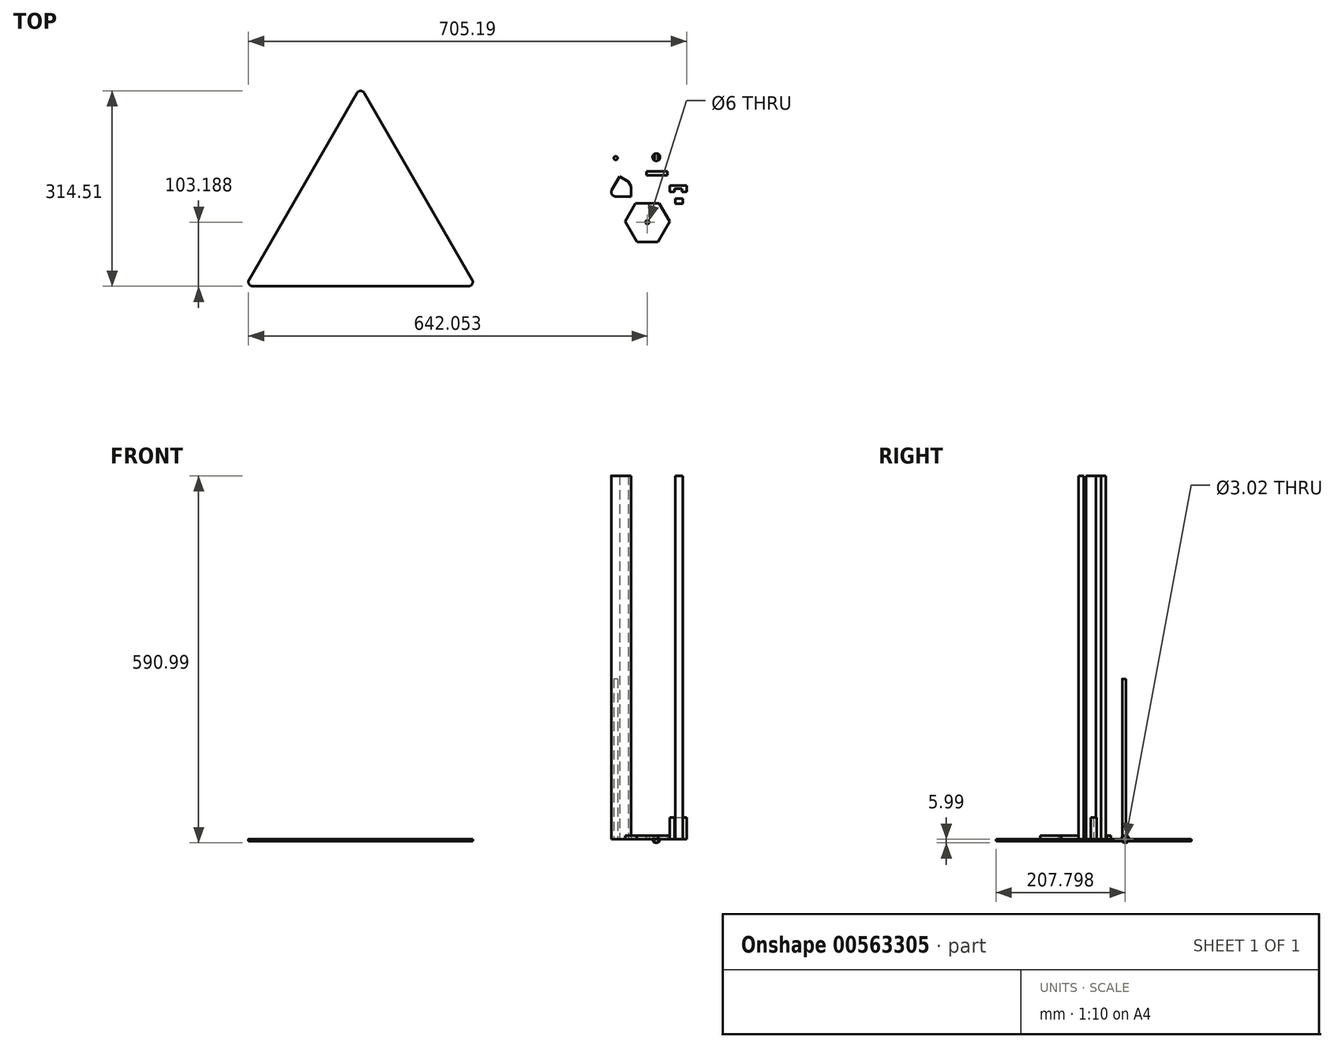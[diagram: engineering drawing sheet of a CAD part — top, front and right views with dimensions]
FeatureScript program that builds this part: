
annotation { "Feature Type Name" : "Feature", "Feature Type Description" : "" }
export const myFeature = defineFeature(function(context is Context, id is Id, definition is map)
    precondition{}
    {
        {
            var Q0;
            Q0=qCreatedBy(makeId("Top.planeOp"),FACE);
            var sketch = newSketch(context, id + "F0", { "sketchPlane" : qUnion([Q0])});
            skLineSegment(sketch, "E0", {"start": v(-31.56, -27.8) * mm, "end": v(-6.56, -27.8) * mm});
            skLineSegment(sketch, "E1", {"start": v(-37.63, -17.3) * mm, "end": v(-25.13, 4.35) * mm});
            skPoint(sketch, "E2.visualSharp", {"position": v(-43.69, -27.8) * mm});
            skArc(sketch, "E2.filletArc", {"start": v(-37.63, -17.3) * mm, "mid": v(-37.63, -24.3) * mm, "end": v(-31.56, -27.8) * mm});
            skLineSegment(sketch, "E3", {"start": v(-6.56, -27.8) * mm, "end": v(-6.56, -11.8) * mm});
            skLineSegment(sketch, "E4", {"start": v(-25.13, 4.35) * mm, "end": v(-11.27, -3.65) * mm});
            skLineSegment(sketch, "E5", {"start": v(-11.27, -3.65) * mm, "end": v(-6.56, -11.8) * mm});
            skSolve(sketch);
        }
        {
            var Q0;
            Q0=makeQuery(id+"F0.imprint","IMPRINT",FACE,{"disambiguationData":[TD([[makeQuery(id+"F0.imprint","IMPRINT",EDGE,{"derivedFrom":sQuery(id+"F0.wireOp",EDGE,"E0")}),1.0]])]});
            extrude(context, id + "F1", {"entities" : qUnion([Q0]), "depth" : 585 * mm, "offsetDistance" : 25 * mm});
        }
        {
            var Q0;
            Q0=qCreatedBy(makeId("Top.planeOp"),FACE);
            var sketch = newSketch(context, id + "F2", { "sketchPlane" : qUnion([Q0])});
            skLineSegment(sketch, "E6.bottom", {"start": v(64.17, -31.27) * mm, "end": v(76.17, -31.27) * mm});
            skLineSegment(sketch, "E6.top", {"start": v(64.17, -39.27) * mm, "end": v(76.17, -39.27) * mm});
            skLineSegment(sketch, "E6.left", {"start": v(64.17, -31.27) * mm, "end": v(64.17, -39.27) * mm});
            skLineSegment(sketch, "E6.right", {"start": v(76.17, -31.27) * mm, "end": v(76.17, -39.27) * mm});
            skSolve(sketch);
        }
        {
            var Q0;
            Q0 = qSketchRegion(id + "F2", true);
            extrude(context, id + "F3", {"entities" : qUnion([Q0]), "depth" : 585 * mm, "offsetDistance" : 25 * mm});
        }
        {
            var Q0;
            Q0=qCreatedBy(makeId("Top.planeOp"),FACE);
            var sketch = newSketch(context, id + "F4", { "sketchPlane" : qUnion([Q0])});
            skLineSegment(sketch, "E7.bottom", {"start": v(55.7, -10.12) * mm, "end": v(82.7, -10.12) * mm});
            skLineSegment(sketch, "E7.left", {"start": v(55.7, -10.12) * mm, "end": v(55.7, -20.12) * mm});
            skLineSegment(sketch, "E7.right", {"start": v(82.7, -10.12) * mm, "end": v(82.7, -20.12) * mm});
            skLineSegment(sketch, "E8", {"start": v(63.2, -20.12) * mm, "end": v(63.2, -15.12) * mm});
            skLineSegment(sketch, "E9", {"start": v(75.2, -15.12) * mm, "end": v(75.2, -20.12) * mm});
            skLineSegment(sketch, "E10", {"start": v(63.2, -15.12) * mm, "end": v(75.2, -15.12) * mm});
            skLineSegment(sketch, "E11", {"start": v(55.7, -20.12) * mm, "end": v(63.2, -20.12) * mm});
            skLineSegment(sketch, "E12", {"start": v(75.2, -20.12) * mm, "end": v(82.7, -20.12) * mm});
            skSolve(sketch);
        }
        {
            var Q0;
            Q0=makeQuery(id+"F4.imprint","IMPRINT",FACE,{"disambiguationData":[TD([[makeQuery(id+"F4.imprint","IMPRINT",EDGE,{"derivedFrom":sQuery(id+"F4.wireOp",EDGE,"E7.bottom")}),-1.0]])]});
            extrude(context, id + "F5", {"entities" : qUnion([Q0]), "depth" : 34.7 * mm, "offsetDistance" : 25 * mm});
        }
        {
            var Q0;
            Q0=qCreatedBy(makeId("Top.planeOp"),FACE);
            var sketch = newSketch(context, id + "F6", { "sketchPlane" : qUnion([Q0])});
            skCircle(sketch, "E13", {"center": v(33.81, 35.39) * mm, "radius": 6 * mm});
            skLineSegment(sketch, "E14.bottom", {"start": v(36.81, 24.39) * mm, "end": v(30.81, 24.39) * mm});
            skLineSegment(sketch, "E14.top", {"start": v(36.81, 46.39) * mm, "end": v(30.81, 46.39) * mm});
            skLineSegment(sketch, "E14.left", {"start": v(36.81, 24.39) * mm, "end": v(36.81, 46.39) * mm});
            skLineSegment(sketch, "E14.right", {"start": v(30.81, 24.39) * mm, "end": v(30.81, 46.39) * mm});
            skLineSegment(sketch, "E15.bottom", {"start": v(36.81, 36.89) * mm, "end": v(30.81, 36.89) * mm});
            skLineSegment(sketch, "E15.top", {"start": v(36.81, 33.89) * mm, "end": v(30.81, 33.89) * mm});
            skLineSegment(sketch, "E15.left", {"start": v(36.81, 36.89) * mm, "end": v(36.81, 33.89) * mm});
            skLineSegment(sketch, "E15.right", {"start": v(30.81, 36.89) * mm, "end": v(30.81, 33.89) * mm});
            skLineSegment(sketch, "E16", {"start": v(27.81, 35.38) * mm, "end": v(42.26, 35.38) * mm, "construction": true});
            skSolve(sketch);
        }
        {
            var Q0;
            {var subQ5=sQuery(id+"F6.wireOp",EDGE,"E15.bottom");Q0=makeQuery(id+"F6.imprint","IMPRINT",FACE,{"disambiguationData":[TD([[makeQuery(id+"F6.imprint","IMPRINT",EDGE,{"derivedFrom":subQ5}),-1.0]])]});}
            var Q1;
            Q1=sQuery(id+"F6.wireOp",EDGE,"E16");
            revolve(context, id + "F7", {"entities" : qUnion([Q0]), "axis" : qUnion([Q1]), "revolveType" : RevolveType.FULL});
        }
        {
            var Q0;
            Q0=qCreatedBy(makeId("Top.planeOp"),FACE);
            var sketch = newSketch(context, id + "F8", { "sketchPlane" : qUnion([Q0])});
            skCircle(sketch, "E17", {"center": v(-31.41, 33.89) * mm, "radius": 3 * mm});
            skSolve(sketch);
        }
        {
            var Q0;
            Q0=makeQuery(id+"F8.imprint","IMPRINT",FACE,{"disambiguationData":[TD([[makeQuery(id+"F8.imprint","IMPRINT",EDGE,{"derivedFrom":sQuery(id+"F8.wireOp",EDGE,"E17")}),1.0]])]});
            extrude(context, id + "F9", {"entities" : qUnion([Q0]), "depth" : 258 * mm, "offsetDistance" : 25 * mm});
        }
        {
            var Q0;
            Q0=qCreatedBy(makeId("Top.planeOp"),FACE);
            var sketch = newSketch(context, id + "F10", { "sketchPlane" : qUnion([Q0])});
            skLineSegment(sketch, "E18.bottom", {"start": v(51.8, 6.41) * mm, "end": v(17.8, 6.41) * mm});
            skLineSegment(sketch, "E18.top", {"start": v(51.8, 12.41) * mm, "end": v(17.8, 12.41) * mm});
            skLineSegment(sketch, "E18.left", {"start": v(51.8, 6.41) * mm, "end": v(51.8, 12.41) * mm});
            skLineSegment(sketch, "E18.right", {"start": v(17.8, 6.41) * mm, "end": v(17.8, 12.41) * mm});
            skPoint(sketch, "E18.middle", {"position": v(34.8, 9.41) * mm});
            skSolve(sketch);
        }
        {
            var Q0;
            Q0=makeQuery(id+"F10.imprint","IMPRINT",FACE,{"disambiguationData":[TD([[makeQuery(id+"F10.imprint","IMPRINT",EDGE,{"derivedFrom":sQuery(id+"F10.wireOp",EDGE,"E18.bottom")}),-1.0]])]});
            extrude(context, id + "F11", {"entities" : qUnion([Q0]), "depth" : 6 * mm, "offsetDistance" : 25 * mm});
        }
        {
            var Q0;
            Q0=qCreatedBy(makeId("Top.planeOp"),FACE);
            var sketch = newSketch(context, id + "F12", { "sketchPlane" : qUnion([Q0])});
            skLineSegment(sketch, "E19", {"start": v(2.57, -100.99) * mm, "end": v(36.57, -100.99) * mm});
            skLineSegment(sketch, "E20", {"start": v(36.57, -100.99) * mm, "end": v(55.57, -68.08) * mm});
            skLineSegment(sketch, "E21", {"start": v(55.57, -68.08) * mm, "end": v(38.57, -38.63) * mm});
            skLineSegment(sketch, "E22", {"start": v(38.57, -38.63) * mm, "end": v(0.57, -38.63) * mm});
            skLineSegment(sketch, "E23", {"start": v(0.57, -38.63) * mm, "end": v(-16.43, -68.08) * mm});
            skLineSegment(sketch, "E24", {"start": v(-16.43, -68.08) * mm, "end": v(2.57, -100.99) * mm});
            skLineSegment(sketch, "E25", {"start": v(19.57, -38.63) * mm, "end": v(19.57, -100.99) * mm, "construction": true});
            skLineSegment(sketch, "E26", {"start": v(-6.93, -84.53) * mm, "end": v(47.07, -53.35) * mm, "construction": true});
            skLineSegment(sketch, "E27", {"start": v(-7.93, -53.35) * mm, "end": v(46.07, -84.53) * mm, "construction": true});
            skPoint(sketch, "E28", {"position": v(19.57, -69.23) * mm});
            skCircle(sketch, "E29", {"center": v(19.57, -69.23) * mm, "radius": 3 * mm});
            skSolve(sketch);
        }
        {
            var Q0;
            Q0 = qSketchRegion(id + "F12", true);
            extrude(context, id + "F13", {"entities" : qUnion([Q0]), "depth" : 6 * mm, "offsetDistance" : 25 * mm});
        }
        {
            var Q0;
            Q0=qCreatedBy(makeId("Top.planeOp"),FACE);
            var sketch = newSketch(context, id + "F14", { "sketchPlane" : qUnion([Q0])});
            skLineSegment(sketch, "E30", {"start": v(-448.04, 138.6) * mm, "end": v(-460.54, 116.94) * mm});
            skLineSegment(sketch, "E31", {"start": v(-435.92, 138.6) * mm, "end": v(-423.42, 116.94) * mm});
            skPoint(sketch, "E32.visualSharp", {"position": v(-441.98, 149.1) * mm});
            skArc(sketch, "E32.filletArc", {"start": v(-435.92, 138.6) * mm, "mid": v(-441.98, 142.1) * mm, "end": v(-448.04, 138.6) * mm});
            skLineSegment(sketch, "E33", {"start": v(-460.54, 116.94) * mm, "end": v(-446.69, 108.94) * mm});
            skLineSegment(sketch, "E34", {"start": v(-423.42, 116.94) * mm, "end": v(-437.28, 108.94) * mm});
            skLineSegment(sketch, "E35", {"start": v(-437.28, 108.94) * mm, "end": v(-446.69, 108.94) * mm});
            skLineSegment(sketch, "E36", {"start": v(-615.48, -172.42) * mm, "end": v(-590.48, -172.42) * mm});
            skLineSegment(sketch, "E37", {"start": v(-621.54, -161.92) * mm, "end": v(-609.04, -140.27) * mm});
            skPoint(sketch, "E38.visualSharp", {"position": v(-627.6, -172.42) * mm});
            skArc(sketch, "E38.filletArc", {"start": v(-621.54, -161.92) * mm, "mid": v(-621.54, -168.92) * mm, "end": v(-615.48, -172.42) * mm});
            skLineSegment(sketch, "E39", {"start": v(-590.48, -172.42) * mm, "end": v(-590.48, -156.42) * mm});
            skLineSegment(sketch, "E40", {"start": v(-609.04, -140.27) * mm, "end": v(-595.19, -148.27) * mm});
            skLineSegment(sketch, "E41", {"start": v(-595.19, -148.27) * mm, "end": v(-590.48, -156.42) * mm});
            skLineSegment(sketch, "E42", {"start": v(-262.42, -161.92) * mm, "end": v(-274.92, -140.27) * mm});
            skLineSegment(sketch, "E43", {"start": v(-268.48, -172.42) * mm, "end": v(-293.48, -172.42) * mm});
            skPoint(sketch, "E44.visualSharp", {"position": v(-256.36, -172.42) * mm});
            skArc(sketch, "E44.filletArc", {"start": v(-268.48, -172.42) * mm, "mid": v(-262.42, -168.92) * mm, "end": v(-262.42, -161.92) * mm});
            skLineSegment(sketch, "E45", {"start": v(-274.92, -140.27) * mm, "end": v(-288.78, -148.27) * mm});
            skLineSegment(sketch, "E46", {"start": v(-293.48, -172.42) * mm, "end": v(-293.48, -156.42) * mm});
            skLineSegment(sketch, "E47", {"start": v(-293.48, -156.42) * mm, "end": v(-288.78, -148.27) * mm});
            skLineSegment(sketch, "E48", {"start": v(-590.48, -172.42) * mm, "end": v(-293.48, -172.42) * mm});
            skLineSegment(sketch, "E49", {"start": v(-609.04, -140.27) * mm, "end": v(-460.54, 116.94) * mm});
            skLineSegment(sketch, "E50", {"start": v(-274.92, -140.27) * mm, "end": v(-423.42, 116.94) * mm});
            skSolve(sketch);
        }
        {
            var Q0;
            Q0 = qSketchRegion(id + "F14", true);
            extrude(context, id + "F15", {"entities" : qUnion([Q0]), "oppositeDirection" : true, "depth" : 3 * mm, "offsetDistance" : 25 * mm});
        }
        {
            var Q0;
            Q0 = qSketchRegion(id + "F12", true);
            extrude(context, id + "F16", {"entities" : qUnion([Q0]), "operationType" : NewBodyOperationType.ADD, "depth" : 1 * mm, "offsetDistance" : 25 * mm});
        }
    });
